FCSTD DOCUMENT  (FreeCAD 0.20R26155 (Git))
Label: TS-1187A-B-A-B
License: All rights reserved
LicenseURL: http://en.wikipedia.org/wiki/All_rights_reserved
objects: Sketcher::SketchObject×2, PartDesign::Body×1
note: 3 computed .brp shape members not serialized (recipe doc carries the construction recipe); baked Part::Feature solids carry a one-line shape summary decoded from their .brp

FEATURE [Sketcher::SketchObject] Sketch  label="Pads_TH_SMD"
  FullyConstrained = true
  MapMode = 5
  Support = -> [XY_Plane]
  sketch-geometry (24):
    g0: LineSegment StartX=-2.5 StartY=1.5 StartZ=0 EndX=2.5 EndY=1.5 EndZ=0
    g1: LineSegment StartX=2.5 StartY=1.5 StartZ=0 EndX=2.5 EndY=-1.5 EndZ=0
    g2: LineSegment StartX=2.5 StartY=-1.5 StartZ=0 EndX=-2.5 EndY=-1.5 EndZ=0
    g3: LineSegment StartX=-2.5 StartY=-1.5 StartZ=0 EndX=-2.5 EndY=1.5 EndZ=0
    g4: LineSegment StartX=-2.5 StartY=1.5 StartZ=0 EndX=-3.5 EndY=1.5 EndZ=0
    g5: LineSegment StartX=-3.5 StartY=1.5 StartZ=0 EndX=-3.5 EndY=2.25 EndZ=0
    g6: LineSegment StartX=-3.5 StartY=2.25 StartZ=0 EndX=-2.5 EndY=2.25 EndZ=0
    g7: LineSegment StartX=-2.5 StartY=2.25 StartZ=0 EndX=-2.5 EndY=1.5 EndZ=0
    g8: LineSegment StartX=2.5 StartY=1.5 StartZ=0 EndX=3.5 EndY=1.5 EndZ=0
    g9: LineSegment StartX=3.5 StartY=1.5 StartZ=0 EndX=3.5 EndY=2.25 EndZ=0
    g10: LineSegment StartX=3.5 StartY=2.25 StartZ=0 EndX=2.5 EndY=2.25 EndZ=0
    g11: LineSegment StartX=2.5 StartY=2.25 StartZ=0 EndX=2.5 EndY=1.5 EndZ=0
    g12: LineSegment StartX=2.5 StartY=-1.5 StartZ=0 EndX=3.5 EndY=-1.5 EndZ=0
    g13: LineSegment StartX=3.5 StartY=-1.5 StartZ=0 EndX=3.5 EndY=-2.25 EndZ=0
    g14: LineSegment StartX=3.5 StartY=-2.25 StartZ=0 EndX=2.5 EndY=-2.25 EndZ=0
    g15: LineSegment StartX=2.5 StartY=-2.25 StartZ=0 EndX=2.5 EndY=-1.5 EndZ=0
    g16: LineSegment StartX=-2.5 StartY=-1.5 StartZ=0 EndX=-3.5 EndY=-1.5 EndZ=0
    g17: LineSegment StartX=-3.5 StartY=-1.5 StartZ=0 EndX=-3.5 EndY=-2.25 EndZ=0
    g18: LineSegment StartX=-3.5 StartY=-2.25 StartZ=0 EndX=-2.5 EndY=-2.25 EndZ=0
    g19: LineSegment StartX=-2.5 StartY=-2.25 StartZ=0 EndX=-2.5 EndY=-1.5 EndZ=0
    g20: LineSegment StartX=-2.5 StartY=-2.25 StartZ=0 EndX=2.5 EndY=-2.25 EndZ=0
    g21: LineSegment StartX=-2.5 StartY=2.25 StartZ=0 EndX=2.5 EndY=2.25 EndZ=0
    g22: LineSegment StartX=3.5 StartY=1.5 StartZ=0 EndX=3.5 EndY=-1.5 EndZ=0
    g23: LineSegment StartX=-3.5 StartY=1.5 StartZ=0 EndX=-3.5 EndY=-1.5 EndZ=0
  constraints (60):
    c: Coincident(g0,g1)
    c: Coincident(g1,g2)
    c: Coincident(g2,g3)
    c: Coincident(g3,g0)
    c: Horizontal(g0)
    c: Vertical(g3)
    c: Coincident(g4,g5)
    c: Coincident(g5,g6)
    c: Coincident(g6,g7)
    c: Coincident(g7,g4)
    c: Horizontal(g4)
    c: Horizontal(g6)
    c: Vertical(g5)
    c: Vertical(g7)
    c: Coincident(g4,g0)
    c: Coincident(g8,g9)
    c: Coincident(g9,g10)
    c: Coincident(g10,g11)
    c: Coincident(g11,g8)
    c: Horizontal(g8)
    c: Horizontal(g10)
    c: Vertical(g9)
    c: Vertical(g11)
    c: Coincident(g8,g0)
    c: Coincident(g12,g13)
    c: Coincident(g13,g14)
    c: Coincident(g14,g15)
    c: Coincident(g15,g12)
    c: Horizontal(g12)
    c: Horizontal(g14)
    c: Vertical(g13)
    c: Vertical(g15)
    c: Coincident(g12,g1)
    c: Coincident(g16,g17)
    c: Coincident(g17,g18)
    c: Coincident(g18,g19)
    c: Coincident(g19,g16)
    c: Horizontal(g16)
    c: Horizontal(g18)
    c: Vertical(g17)
    c: Vertical(g19)
    c: Coincident(g16,g2)
    c: Symmetric(g8,g12,g-1)
    c: Symmetric(g16,g12,g-2)
    c: Coincident(g20,g18)
    c: Coincident(g20,g14)
    c: Coincident(g21,g6)
    c: Coincident(g21,g10)
    c: Coincident(g22,g8)
    c: Coincident(g22,g12)
    c: Coincident(g23,g4)
    c: Coincident(g23,g16)
    c: Vertical(g23)
    c: Horizontal(g21)
    c: DistanceX(g21,g21) = 5
    c: DistanceX(g5,g9) = 7
    c: DistanceY(g22,g22) = 3
    c: DistanceY(g13,g9) = 4.5
    c: Symmetric(g13,g17,g-2)
    c: Symmetric(g9,g13,g-1)
FEATURE [Sketcher::SketchObject] Sketch001  label="F_CrtYd_+_0.05"
  FullyConstrained = true
  MapMode = 5
  Support = -> [XY_Plane]
  sketch-geometry (4):
    g0: LineSegment StartX=-2.6 StartY=2.6 StartZ=0 EndX=2.6 EndY=2.6 EndZ=0
    g1: LineSegment StartX=2.6 StartY=2.6 StartZ=0 EndX=2.6 EndY=-2.6 EndZ=0
    g2: LineSegment StartX=2.6 StartY=-2.6 StartZ=0 EndX=-2.6 EndY=-2.6 EndZ=0
    g3: LineSegment StartX=-2.6 StartY=-2.6 StartZ=0 EndX=-2.6 EndY=2.6 EndZ=0
  constraints (10):
    c: Coincident(g0,g1)
    c: Coincident(g1,g2)
    c: Coincident(g2,g3)
    c: Coincident(g3,g0)
    c: Horizontal(g2)
    c: Vertical(g3)
    c: Symmetric(g0,g1,g-1)
    c: Symmetric(g0,g0,g-2)
    c: DistanceX(g0,g0) = 5.2
    c: DistanceY(g1,g1) = 5.2
FEATURE [PartDesign::Body] Body
  Group = -> [Sketch,Sketch001]
  Origin = -> Origin
